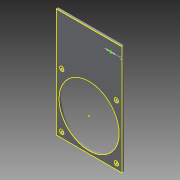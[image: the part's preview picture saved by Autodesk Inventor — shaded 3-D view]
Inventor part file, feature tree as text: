
AUTODESK INVENTOR PART (.ipt)
format: ipt  version: 2014 (Build 180170000, 170)  size: 109,056 bytes
history: native  units: mm
features: sketch x4, extrude x3
ambient origin geometry x8: Origin, YZ Plane, XZ Plane, XY Plane, X Axis, Y Axis, Z Axis, Center Point
bodies: Solid1 (feature_tree)
feature tree (7):
  extrude  "Extrusion1"  Depth=60.0mm
  extrude  "Extrusion2"  Depth=2.0mm
  extrude  "Extrusion4"  Depth=10.0mm
  sketch  "Sketch5"  dims[d42=20.0mm d44=50.0mm d45=20.0mm d47=50.0mm d50=55.0mm d52=30.0mm d53=30.0mm d54=10.0mm d55=0.0mm d56=55.0mm d57=2.0mm]
  sketch  "Sketch1"  dims[d0=100.0mm d1=60.0mm]
  sketch  "Sketch2"  dims[d2=2.0mm d3=0.0mm d7=4.0mm]
  sketch  "Sketch4"  dims[d8=10.0mm d9=0.0mm d40=5.0mm]
